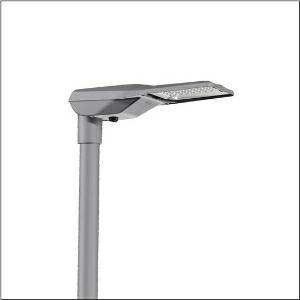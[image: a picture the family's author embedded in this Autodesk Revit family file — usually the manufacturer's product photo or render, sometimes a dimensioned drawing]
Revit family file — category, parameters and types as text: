
# Revit family: streetlight_sl_21_iq_mini___p0_5a_5xe2v31u08gb_e20a
name_source: partatom
category: Lighting Fixtures
units: mm (PartAtom-declared; Revit-internal decimal feet)

## family parameters
Cut with Voids When Loaded = No
Host = Face
Light Source = No
Part Type = Normal
Room Calculation Point = No
Round Connector Dimension = Use Diameter
Shared = No

## types (1)
- --- (1 x LED, 5880 lm, 39.8 W, 3000K)
    Apparent Load = 40 VA
    CIE Flux Codes = 37 73 96 100 100
    Color Rendering = 70
    Color Temperature = 3000K
    Default Elevation = 1800 mm
    Description = Streetlight SL 21 iQ mini, mast luminaire, primary light control with lens, of PMMA, primary optical cover: cover, of toughened safety glass, transparent, light distribution: P0.5a, light emission: direct distribution, primary light characteristic: asymmetric, installation type: post-top, side-entry, LED, High Power LED, rated luminous flux: 5.880lm, luminous efficacy: 148lm/W, light colour: 730, colour temperature: 3000K, control gear: iQ-Street Remote, D4i with power reduction, control: pre-setting: logarithmic dimming characteristic, Street-Remote, Auto-Match, Temp-Guard, Lumen-Switch, Night-Set, Smart-Wire, Light-Fading, Desk-Remote (wireless, voltage-free reading and setting of iQ features in the workshop via application-optimized NFC function/RFID function), optimised constant luminous flux control (CLO 2.0), mains connection: 220..240V, AC, 50/60Hz, start of lifetime: 40W, end of service life: 41W, reduction: 18W, luminaire housing, of diecast aluminium, powder-coated, SITECO metallic grey (DB 702S), corrosivity category C5 high according to DIN EN ISO 12944, please order mast flange separately, inclination adjustable: 0°, 5°, 10°, 15°, sealing non-destructively replaceable, multi-level sealing system, length: 628mm, width: 235mm, height: 110mm, mast flange for spigot size: 42mm (side-entry): 5XC10008XM4, 60/48mm (side-entry/post-top): 5XC10108XM2, 76/60mm (side-entry/post-top): 5XC10108XM1, mounting height: 4..8m, Smart Interface below, protection rating (complete): IP66, insulation class (complete): insulation class II (safety insulation), certification: CE, ENEC, ENEC+, VDE, impact resistance: IK10, permissible operating ambient temperature for outdoor applications: -40..+50°C, standard-compliant lighting for roads and squares, packaging unit: 1 piece

Light Distribution: P0.5a
    Height = 110 mm
    Lamp = 1 x LED
    Lamp Light Flux = 5880 lm
    Lamp Power = 39.8 W
    Lamp count = 1
    Length = 625 mm
    Luminous efficacy = 148 lm/W
    Manufacturer = Siteco
    ModVariant = No
    Model = 5XE2V31U08GB
    Number of Poles = 1
    OnlyDefault = Yes
    Power Factor = 1
    Product Name = Streetlight SL 21 iQ mini | P0.5a
    Product group = mast luminaire | pylon top
    ProductGroupID = 6100
    Protection Class = Protection class II
    Protection Degree = IP 66
    RLX_Detail_Level = 1
    RLX_Emergency_Light_Flux = 0 lm
    RLX_Emergency_Type = 0
    RLX_Emergency_Type_DB = No
    RlxData = <blob elided: 92037 chars, md5=8660bc4f>
    Socket = socket
    Standby Power = 0 W
    System Light Flux = 5880 lm
    System Power = 40 W
    Type Comments = factory setting: luminous flux: 100 % | dim-lin: 254 | 800 mA
    Type Image = l_1003516.jpg
    URL = http://relux.com
    VarID = @adj_078491
    Voltage = 0 V
    Weight = 0.00 kg
    Width = 234 mm

## geometry (parser evidence)
native form markers: Blend x4, Sweep x11
no freeform markers — native parametric forms only
